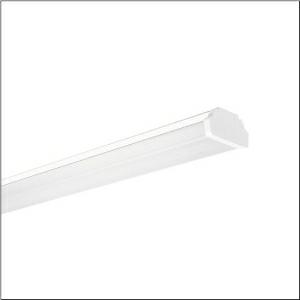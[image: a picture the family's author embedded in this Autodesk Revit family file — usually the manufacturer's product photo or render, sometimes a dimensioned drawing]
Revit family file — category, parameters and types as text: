
# Revit family: dus_r__31_gen_2_53bd811dv4d5d2_21da
name_source: partatom
category: Lighting Fixtures
units: mm (PartAtom-declared; Revit-internal decimal feet)

## family parameters
Cut with Voids When Loaded = No
Host = Face
Light Source = No
Part Type = Normal
Room Calculation Point = No
Round Connector Dimension = Use Diameter
Shared = No

## types (1)
- --- (1 x LED, 13680 lm, 74.9 W, 4000K)
    Apparent Load = 75 VA
    CIE Flux Codes = 50 78 94 90 100
    Color Rendering = 80
    Color Temperature = 4000K
    Default Elevation = 1800 mm
    Description = DUS® 31 Gen.2, luminaire insert, of sheet steel, coil coated, white, length: 1.535mm, width: 81mm, height: 90mm, 5x system unit, system units: 307mm, LED rated luminous flux: 13.680lm, light colour: 840, control gear: DALI 2, control gear: ECG DALI, with plug, 5-pole, with phase selection, mains connection: 220..240V, AC, 50/60Hz, rated input power: 75W, through-wiring accessed according to module size, primary optical cover: cover, of PMMA, light emission: direct distribution, primary light characteristic: symmetric, protection rating (complete): IP20, protection rating (LED compartment): IP50, insulation class (complete): insulation class I (protective earthing), certification: CE, ENEC, VDE, UKCA, impact resistance: IK03, permissible ambient temperature for indoor applications: -25..+35°C, corresponds to IFS (International Featured Standards) requirements for safety and quality in the food industry, reducing of maximum allowable ambient temperature of 5°C with ceiling mounting, packaging unit: 1 piece
    Height = 95 mm
    Lamp = 1 x LED
    Lamp Light Flux = 13680 lm
    Lamp Power = 74.9 W
    Lamp count = 1
    Length = 1535 mm
    Luminous efficacy = 183 lm/W
    Manufacturer = Siteco
    ModVariant = No
    Model = 53BD811DV4D5D2
    Mounting Place = Ceiling
    Mounting Type = Pendant
    Number of Poles = 1
    OnlyDefault = Yes
    Power Factor = 1
    Product Name = DUS® 31 Gen.2
    Product group = luminaire insert | ceiling pendant
    ProductGroupID = 902
    Protection Class = Protection class I
    Protection Degree = IP 20
    RLX_Detail_Level = 1
    RLX_Emergency_Light_Flux = 0 lm
    RLX_Emergency_Type = 0
    RLX_Emergency_Type_DB = No
    RlxData = <blob elided: 32253 chars, md5=7ce66c71>
    Socket = socket
    Standby Power = 0 W
    System Light Flux = 13680 lm
    System Power = 75 W
    Type Comments = factory setting: luminous flux: 100 % | dim-lin: 254 | 511 mA
    Type Image = l_1319596.jpg
    URL = http://relux.com
    VarID = @adj_063663
    Voltage = 0 V
    Weight = 0.00 kg
    Width = 81 mm

## geometry (parser evidence)
native form markers: Blend x4, Sweep x13
no freeform markers — native parametric forms only
